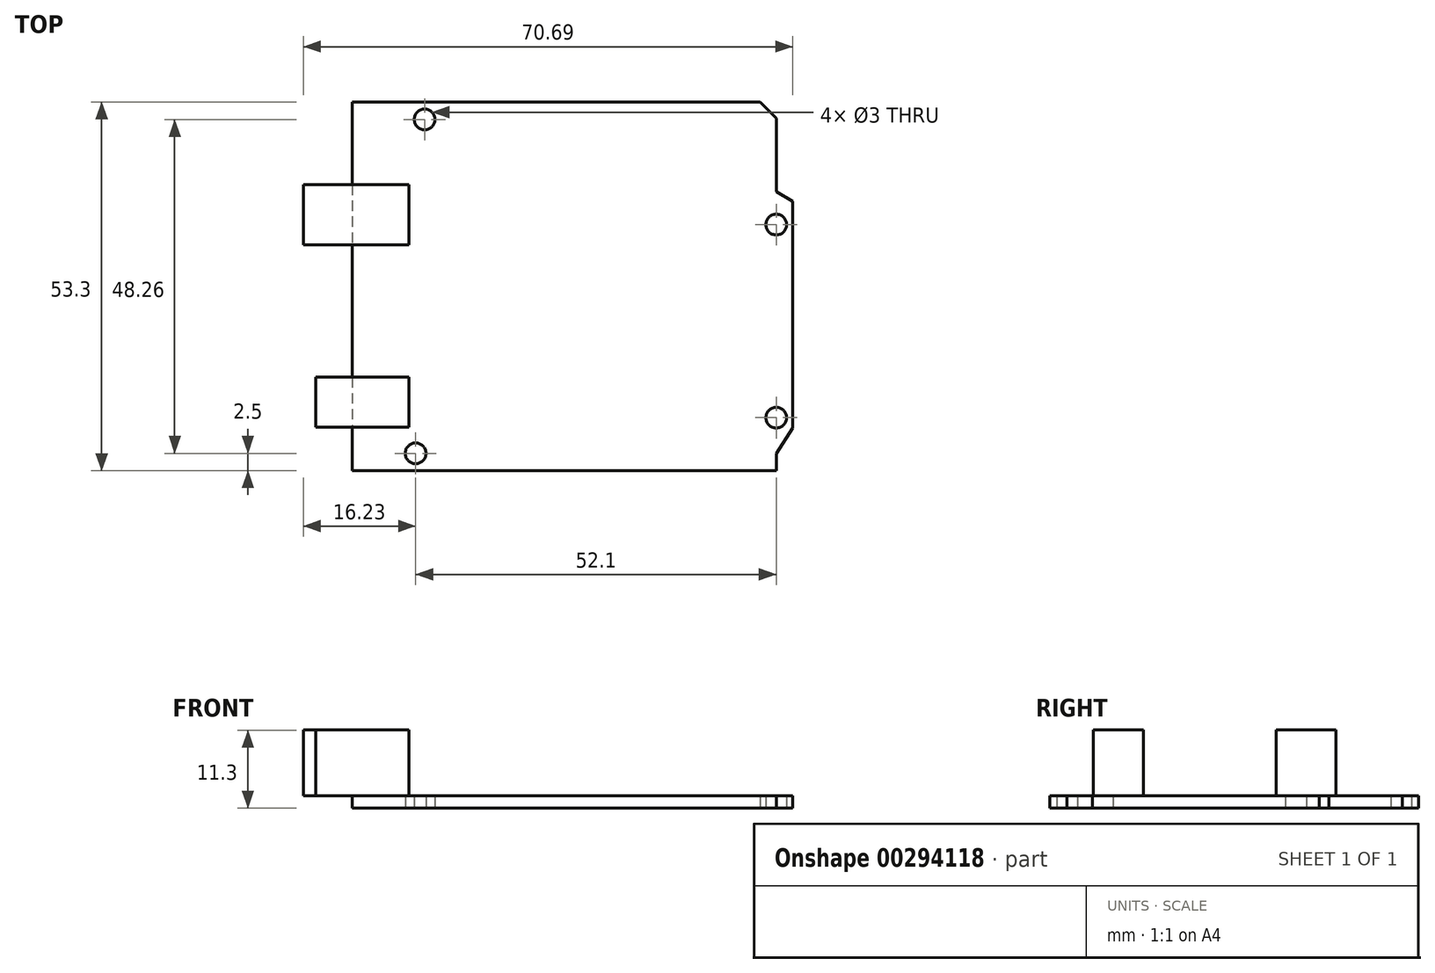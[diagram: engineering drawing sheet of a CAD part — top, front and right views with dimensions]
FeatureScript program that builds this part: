
annotation { "Feature Type Name" : "Feature", "Feature Type Description" : "" }
export const myFeature = defineFeature(function(context is Context, id is Id, definition is map)
    precondition{}
    {
        {
            var Q0;
            Q0=qCreatedBy(makeId("Top.planeOp"),FACE);
            var sketch = newSketch(context, id + "F0", { "sketchPlane" : qUnion([Q0])});
            skLineSegment(sketch, "E0", {"start": v(0, 0) * mm, "end": v(61.27, 0) * mm});
            skLineSegment(sketch, "E1", {"start": v(61.27, 0) * mm, "end": v(61.27, 2.46) * mm});
            skLineSegment(sketch, "E2", {"start": v(0, 53.3) * mm, "end": v(58.91, 53.3) * mm});
            skLineSegment(sketch, "E3", {"start": v(61.27, 50.94) * mm, "end": v(61.27, 40.34) * mm});
            skLineSegment(sketch, "E4", {"start": v(58.91, 53.3) * mm, "end": v(61.27, 50.94) * mm});
            skPoint(sketch, "E5", {"position": v(63.63, 38.93) * mm});
            skLineSegment(sketch, "E6", {"start": v(61.27, 40.34) * mm, "end": v(63.63, 38.93) * mm});
            skCircle(sketch, "E7", {"center": v(9.17, 2.5) * mm, "radius": 1.5 * mm});
            skCircle(sketch, "E8", {"center": v(10.47, 50.76) * mm, "radius": 1.5 * mm});
            skLineSegment(sketch, "E9", {"start": v(63.63, 38.93) * mm, "end": v(63.63, 6.16) * mm});
            skLineSegment(sketch, "E10", {"start": v(63.63, 6.16) * mm, "end": v(61.27, 2.46) * mm});
            skCircle(sketch, "E11", {"center": v(61.27, 35.56) * mm, "radius": 1.5 * mm});
            skCircle(sketch, "E12", {"center": v(61.27, 7.66) * mm, "radius": 1.5 * mm});
            skLineSegment(sketch, "E13", {"start": v(0, 53.3) * mm, "end": v(0, 0) * mm});
            skLineSegment(sketch, "E14", {"start": v(61.27, 46.91) * mm, "end": v(61.27, 1.23) * mm, "construction": true});
            skSolve(sketch);
        }
        {
            var Q0;
            Q0=qSketchRegion(id+"F0",true);
            extrude(context, id + "F1", {"entities" : qUnion([Q0]), "depth" : 1.78 * mm});
        }
        {
            var Q0;
            Q0=makeQuery(id+"F1.opExtrude","CAP_FACE",FACE,{"disambiguationData":[OSD([sQuery(id+"F0.wireOp",EDGE,"E0"),sQuery(id+"F0.wireOp",EDGE,"E1"),sQuery(id+"F0.wireOp",EDGE,"E2"),sQuery(id+"F0.wireOp",EDGE,"E3"),sQuery(id+"F0.wireOp",EDGE,"E4"),sQuery(id+"F0.wireOp",EDGE,"E6"),sQuery(id+"F0.wireOp",EDGE,"E7"),sQuery(id+"F0.wireOp",EDGE,"E8"),sQuery(id+"F0.wireOp",EDGE,"E9"),sQuery(id+"F0.wireOp",EDGE,"E10"),sQuery(id+"F0.wireOp",EDGE,"E11"),sQuery(id+"F0.wireOp",EDGE,"E12"),sQuery(id+"F0.wireOp",EDGE,"E13")])],"isStart":false});
            var sketch = newSketch(context, id + "F2", { "sketchPlane" : qUnion([Q0])});
            skLineSegment(sketch, "E15.bottom", {"start": v(8.2, 41.34) * mm, "end": v(-7.06, 41.34) * mm});
            skLineSegment(sketch, "E15.top", {"start": v(8.2, 32.67) * mm, "end": v(-7.06, 32.67) * mm});
            skLineSegment(sketch, "E15.left", {"start": v(8.2, 41.34) * mm, "end": v(8.2, 32.67) * mm});
            skLineSegment(sketch, "E15.right", {"start": v(-7.06, 41.34) * mm, "end": v(-7.06, 32.67) * mm});
            skLineSegment(sketch, "E16.bottom", {"start": v(8.2, 13.5) * mm, "end": v(-5.23, 13.5) * mm});
            skLineSegment(sketch, "E16.top", {"start": v(8.2, 6.28) * mm, "end": v(-5.23, 6.28) * mm});
            skLineSegment(sketch, "E16.left", {"start": v(8.2, 13.5) * mm, "end": v(8.2, 6.28) * mm});
            skLineSegment(sketch, "E16.right", {"start": v(-5.23, 13.5) * mm, "end": v(-5.23, 6.28) * mm});
            skSolve(sketch);
        }
        {
            var Q0;
            {var subQ0=sQuery(id+"F2.wireOp",EDGE,"E15.right");Q0=makeQuery(id+"F2.imprint","IMPRINT",FACE,{"disambiguationData":[TD([[makeQuery(id+"F2.imprint","IMPRINT",EDGE,{"derivedFrom":subQ0}),1.0]])]});}
            var Q1;
            {var subQ0=sQuery(id+"F2.wireOp",EDGE,"E16.right");Q1=makeQuery(id+"F2.imprint","IMPRINT",FACE,{"disambiguationData":[TD([[makeQuery(id+"F2.imprint","IMPRINT",EDGE,{"derivedFrom":subQ0}),1.0]])]});}
            var Q2;
            {var subQ0=sQuery(id+"F2.wireOp",EDGE,"E15.left");Q2=makeQuery(id+"F2.imprint","IMPRINT",FACE,{"disambiguationData":[TD([[makeQuery(id+"F2.imprint","IMPRINT",EDGE,{"derivedFrom":subQ0}),-1.0]])]});}
            var Q3;
            {var subQ0=sQuery(id+"F2.wireOp",EDGE,"E16.left");Q3=makeQuery(id+"F2.imprint","IMPRINT",FACE,{"disambiguationData":[TD([[makeQuery(id+"F2.imprint","IMPRINT",EDGE,{"derivedFrom":subQ0}),-1.0]])]});}
            extrude(context, id + "F3", {"entities" : qUnion([Q0, Q1, Q2, Q3]), "depth" : 9.52 * mm});
        }
    });
